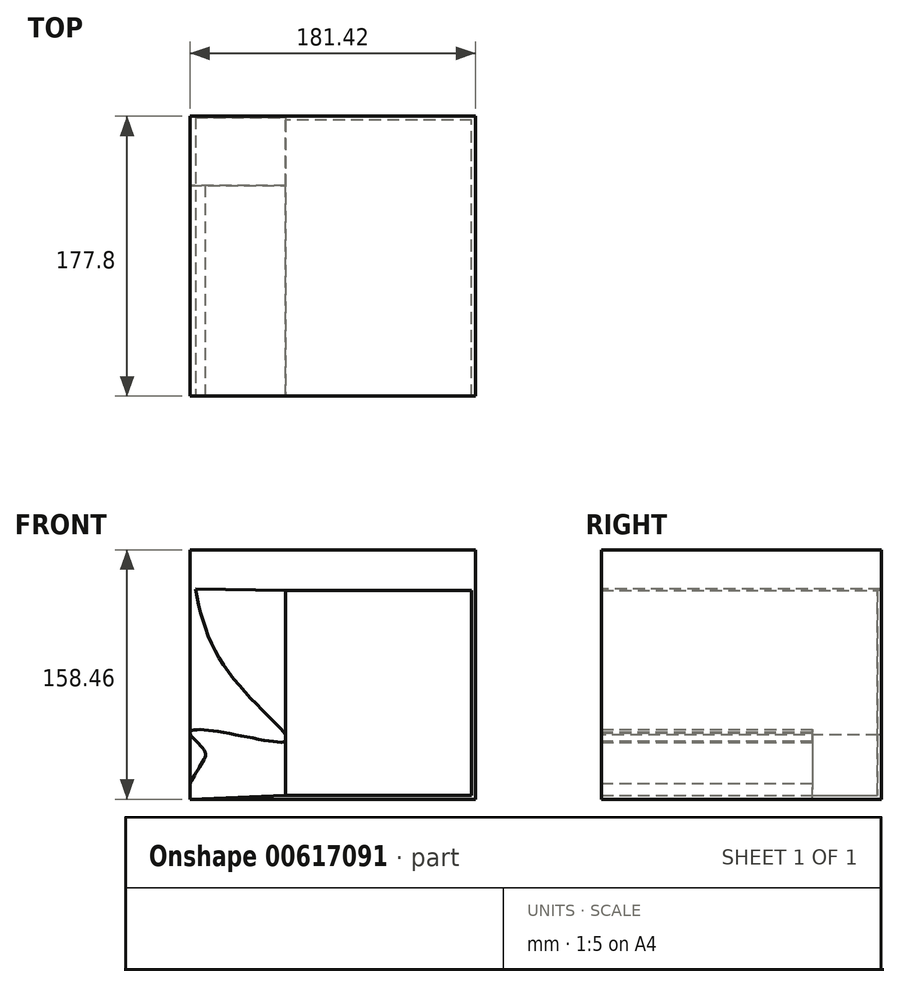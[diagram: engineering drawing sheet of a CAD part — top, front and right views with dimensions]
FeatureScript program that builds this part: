
annotation { "Feature Type Name" : "Feature", "Feature Type Description" : "" }
export const myFeature = defineFeature(function(context is Context, id is Id, definition is map)
    precondition{}
    {
        {
            var Q0;
            Q0=qCreatedBy(makeId("Front.planeOp"),FACE);
            var sketch = newSketch(context, id + "F0", { "sketchPlane" : qUnion([Q0])});
            skLineSegment(sketch, "E0.bottom", {"start": v(90.7, -79.23) * mm, "end": v(-90.7, -79.23) * mm});
            skLineSegment(sketch, "E0.top", {"start": v(90.7, 79.23) * mm, "end": v(-90.7, 79.23) * mm});
            skLineSegment(sketch, "E0.left", {"start": v(90.7, -79.23) * mm, "end": v(90.7, 79.23) * mm});
            skLineSegment(sketch, "E0.right", {"start": v(-90.7, -79.23) * mm, "end": v(-90.7, 79.23) * mm});
            skPoint(sketch, "E0.middle", {"position": v(0, 0) * mm});
            skSolve(sketch);
        }
        {
            var Q0;
            Q0 = qSketchRegion(id + "F0", true);
            extrude(context, id + "F1", {"entities" : qUnion([Q0]), "depth" : 177.8 * mm, "offsetDistance" : 25.4 * mm});
        }
        {
            var Q0;
            Q0=makeQuery(id+"F1.opExtrude","CAP_FACE",FACE,{"disambiguationData":[OSD([sQuery(id+"F0.wireOp",EDGE,"E0.bottom"),sQuery(id+"F0.wireOp",EDGE,"E0.top"),sQuery(id+"F0.wireOp",EDGE,"E0.left"),sQuery(id+"F0.wireOp",EDGE,"E0.right")])],"isStart":false});
            shell(context, id + "F2", {"entities" : qUnion([Q0]), "thickness" : 2.54 * mm});
        }
        {
            var Q0;
            Q0=makeQuery(id+"F2.opShell","OFFSET_FACE",FACE,{"disambiguationData":[OSD([sQuery(id+"F0.wireOp",EDGE,"E0.bottom"),sQuery(id+"F0.wireOp",EDGE,"E0.top"),sQuery(id+"F0.wireOp",EDGE,"E0.left"),sQuery(id+"F0.wireOp",EDGE,"E0.right")])]});
            var sketch = newSketch(context, id + "F3", { "sketchPlane" : qUnion([Q0])});
            skLineSegment(sketch, "E1.bottom", {"start": v(-88.17, 76.7) * mm, "end": v(-29.83, 76.7) * mm});
            skLineSegment(sketch, "E1.top", {"start": v(-88.17, -76.7) * mm, "end": v(-29.83, -76.7) * mm});
            skLineSegment(sketch, "E1.left", {"start": v(-88.17, 76.7) * mm, "end": v(-88.17, -76.7) * mm});
            skLineSegment(sketch, "E1.right", {"start": v(-29.83, 76.7) * mm, "end": v(-29.83, -76.7) * mm});
            skSolve(sketch);
        }
        {
            var Q0;
            Q0 = qSketchRegion(id + "F3", true);
            extrude(context, id + "F4", {"entities" : qUnion([Q0]), "operationType" : NewBodyOperationType.ADD, "depth" : 175.26 * mm, "offsetDistance" : 25.4 * mm});
        }
        {
            var Q0;
            Q0=makeQuery(id+"F2.opShell","OFFSET_FACE",FACE,{"disambiguationData":[OSD([sQuery(id+"F0.wireOp",EDGE,"E0.bottom"),sQuery(id+"F0.wireOp",EDGE,"E0.top"),sQuery(id+"F0.wireOp",EDGE,"E0.left"),sQuery(id+"F0.wireOp",EDGE,"E0.right")])]});
            var sketch = newSketch(context, id + "F5", { "sketchPlane" : qUnion([Q0])});
            skLineSegment(sketch, "E2.bottom", {"start": v(88.17, 76.7) * mm, "end": v(-29.83, 76.7) * mm});
            skLineSegment(sketch, "E2.top", {"start": v(88.17, 53.5) * mm, "end": v(-29.83, 53.5) * mm});
            skLineSegment(sketch, "E2.left", {"start": v(88.17, 76.7) * mm, "end": v(88.17, 53.5) * mm});
            skLineSegment(sketch, "E2.right", {"start": v(-29.83, 76.7) * mm, "end": v(-29.83, 53.5) * mm});
            skSolve(sketch);
        }
        {
            var Q0;
            Q0 = qSketchRegion(id + "F5", true);
            extrude(context, id + "F6", {"entities" : qUnion([Q0]), "operationType" : NewBodyOperationType.ADD, "depth" : 175.26 * mm, "offsetDistance" : 25.4 * mm});
        }
        {
            var Q0;
            Q0=makeQuery(id+"F6.boolean.opBoolean","MERGE",FACE,{"derivedFrom":[makeQuery(id+"F4.boolean.opBoolean","MERGE",FACE,{"derivedFrom":[makeQuery(id+"F1.opExtrude","CAP_FACE",FACE,{"disambiguationData":[OSD([sQuery(id+"F0.wireOp",EDGE,"E0.bottom"),sQuery(id+"F0.wireOp",EDGE,"E0.top"),sQuery(id+"F0.wireOp",EDGE,"E0.left"),sQuery(id+"F0.wireOp",EDGE,"E0.right")])],"isStart":false}),makeQuery(id+"F4.opExtrude","CAP_FACE",FACE,{"disambiguationData":[OSD([sQuery(id+"F3.wireOp",EDGE,"E1.bottom"),sQuery(id+"F3.wireOp",EDGE,"E1.top"),sQuery(id+"F3.wireOp",EDGE,"E1.left"),sQuery(id+"F3.wireOp",EDGE,"E1.right")])],"isStart":false})]}),makeQuery(id+"F6.opExtrude","CAP_FACE",FACE,{"disambiguationData":[OSD([sQuery(id+"F5.wireOp",EDGE,"E2.bottom"),sQuery(id+"F5.wireOp",EDGE,"E2.top"),sQuery(id+"F5.wireOp",EDGE,"E2.left"),sQuery(id+"F5.wireOp",EDGE,"E2.right")])],"isStart":false})]});
            var sketch = newSketch(context, id + "F7", { "sketchPlane" : qUnion([Q0])});
            skFitSpline(sketch, "E3", {"points": [v(-90.7, 79.23) * mm, v(-70.03, 6.98) * mm, v(-29.83, -38.5) * mm, v(-29.83, -42.64) * mm, v(-78.82, -35.4) * mm, v(-90.7, -37.47) * mm, v(-81.4, -48.33) * mm, v(-82.96, -56.08) * mm, v(-90.7, -69.52) * mm, v(-90.7, -71.07) * mm], "startDerivative": vector(44.4, -353.51) * mm, "endDerivative": vector(11.63, -37.43) * mm});
            skLineSegment(sketch, "E4", {"start": v(-90.7, -71.07) * mm, "end": v(-90.7, -79.23) * mm});
            skLineSegment(sketch, "E5", {"start": v(-90.7, -79.23) * mm, "end": v(-29.83, -76.7) * mm});
            skLineSegment(sketch, "E6", {"start": v(-29.83, -76.7) * mm, "end": v(-29.83, 53.5) * mm});
            skLineSegment(sketch, "E7", {"start": v(-29.83, 53.5) * mm, "end": v(-87.56, 54.19) * mm});
            skSolve(sketch);
        }
        {
            var Q0;
            Q0 = qSketchRegion(id + "F7", true);
            extrude(context, id + "F8", {"entities" : qUnion([Q0]), "operationType" : NewBodyOperationType.REMOVE, "oppositeDirection" : true, "depth" : 155.45 * mm, "offsetDistance" : 25.4 * mm});
        }
        {
            var Q0;
            Q0=makeQuery(id+"F8.boolean.opBoolean","COPY",FACE,{"derivedFrom":makeQuery(id+"F8.opExtrude","CAP_FACE",FACE,{"disambiguationData":[OSD([sQuery(id+"F7.wireOp",EDGE,"E3"),sQuery(id+"F7.wireOp",EDGE,"E6"),sQuery(id+"F7.wireOp",EDGE,"E7")])],"isStart":false})});
            extrude(context, id + "F9", {"entities" : qUnion([Q0]), "operationType" : NewBodyOperationType.REMOVE, "oppositeDirection" : true, "depth" : 21.59 * mm, "offsetDistance" : 25.4 * mm});
        }
        {
            var Q0;
            Q0=makeQuery(id+"F8.boolean.opBoolean","COPY",FACE,{"derivedFrom":makeQuery(id+"F8.opExtrude","CAP_FACE",FACE,{"disambiguationData":[OSD([sQuery(id+"F7.wireOp",EDGE,"E3"),sQuery(id+"F7.wireOp",EDGE,"E4"),sQuery(id+"F7.wireOp",EDGE,"E5"),sQuery(id+"F7.wireOp",EDGE,"E6")])],"isStart":false})});
            extrude(context, id + "F10", {"entities" : qUnion([Q0]), "operationType" : NewBodyOperationType.ADD, "depth" : 21.59 * mm, "offsetDistance" : 25.4 * mm});
        }
    });
